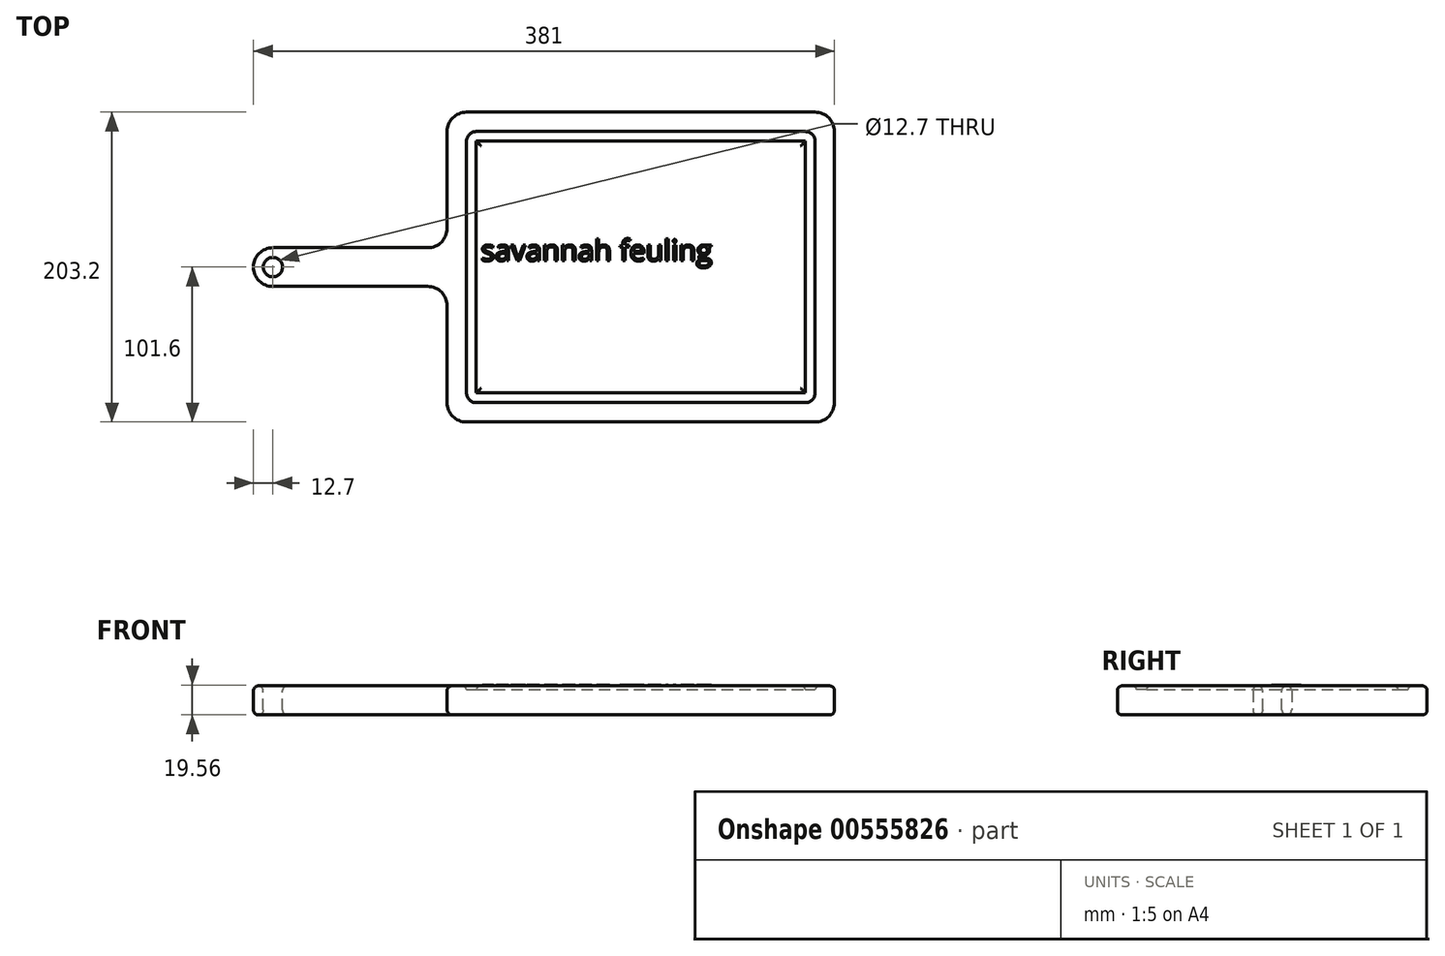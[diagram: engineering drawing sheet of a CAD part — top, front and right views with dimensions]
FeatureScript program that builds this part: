
annotation { "Feature Type Name" : "Feature", "Feature Type Description" : "" }
export const myFeature = defineFeature(function(context is Context, id is Id, definition is map)
    precondition{}
    {
        {
            var Q0;
            Q0=qCreatedBy(makeId("Top.planeOp"),FACE);
            var sketch = newSketch(context, id + "F0", { "sketchPlane" : qUnion([Q0])});
            skLineSegment(sketch, "E0.bottom", {"start": v(0, 0) * mm, "end": v(254, 0) * mm});
            skLineSegment(sketch, "E0.top", {"start": v(0, 203.2) * mm, "end": v(254, 203.2) * mm});
            skLineSegment(sketch, "E0.left", {"start": v(0, 0) * mm, "end": v(0, 203.2) * mm});
            skLineSegment(sketch, "E0.right", {"start": v(254, 0) * mm, "end": v(254, 203.2) * mm});
            skLineSegment(sketch, "E1.bottom", {"start": v(0, 114.3) * mm, "end": v(-127, 114.3) * mm});
            skLineSegment(sketch, "E1.top", {"start": v(0, 88.9) * mm, "end": v(-127, 88.9) * mm});
            skLineSegment(sketch, "E1.left", {"start": v(0, 114.3) * mm, "end": v(0, 88.9) * mm});
            skLineSegment(sketch, "E1.right", {"start": v(-127, 114.3) * mm, "end": v(-127, 88.9) * mm});
            skSolve(sketch);
        }
        {
            var Q0;
            {var subQ3=sQuery(id+"F0.wireOp",EDGE,"E0.bottom");Q0=makeQuery(id+"F0.imprint","IMPRINT",FACE,{"disambiguationData":[TD([[makeQuery(id+"F0.imprint","IMPRINT",EDGE,{"derivedFrom":subQ3}),1.0]])]});}
            var Q1;
            Q1=makeQuery(id+"F0.imprint","IMPRINT",FACE,{"disambiguationData":[TD([[makeQuery(id+"F0.imprint","IMPRINT",EDGE,{"derivedFrom":sQuery(id+"F0.wireOp",EDGE,"E1.bottom")}),1.0]])]});
            extrude(context, id + "F1", {"entities" : qUnion([Q0, Q1]), "depth" : 19.05 * mm, "offsetDistance" : 25.4 * mm});
        }
        {
            var Q0;
            Q0=makeQuery(id+"F1.opExtrude","CAP_FACE",FACE,{"disambiguationData":[OSD([sQuery(id+"F0.wireOp",EDGE,"E0.bottom"),sQuery(id+"F0.wireOp",EDGE,"E0.top"),sQuery(id+"F0.wireOp",EDGE,"E0.left"),sQuery(id+"F0.wireOp",EDGE,"E0.right"),sQuery(id+"F0.wireOp",EDGE,"E1.bottom"),sQuery(id+"F0.wireOp",EDGE,"E1.top"),sQuery(id+"F0.wireOp",EDGE,"E1.right")])],"isStart":false});
            var sketch = newSketch(context, id + "F2", { "sketchPlane" : qUnion([Q0])});
            skCircle(sketch, "E2", {"center": v(-114.3, 101.6) * mm, "radius": 6.35 * mm});
            skSolve(sketch);
        }
        {
            var Q0;
            Q0 = qSketchRegion(id + "F2", true);
            extrude(context, id + "F3", {"entities" : qUnion([Q0]), "operationType" : NewBodyOperationType.REMOVE, "oppositeDirection" : true, "depth" : 25.4 * mm, "offsetDistance" : 25.4 * mm});
        }
        {
            var Q0;
            Q0=makeQuery(id+"F1.opExtrude","CAP_FACE",FACE,{"disambiguationData":[OSD([sQuery(id+"F0.wireOp",EDGE,"E0.bottom"),sQuery(id+"F0.wireOp",EDGE,"E0.top"),sQuery(id+"F0.wireOp",EDGE,"E0.left"),sQuery(id+"F0.wireOp",EDGE,"E0.right"),sQuery(id+"F0.wireOp",EDGE,"E1.bottom"),sQuery(id+"F0.wireOp",EDGE,"E1.top"),sQuery(id+"F0.wireOp",EDGE,"E1.right")])],"isStart":false});
            var sketch = newSketch(context, id + "F4", { "sketchPlane" : qUnion([Q0])});
            skLineSegment(sketch, "E3.0", {"start": v(12.7, 12.7) * mm, "end": v(12.7, 88.9) * mm});
            skLineSegment(sketch, "E3.1", {"start": v(12.7, 114.3) * mm, "end": v(12.7, 190.5) * mm});
            skLineSegment(sketch, "E3.2", {"start": v(12.7, 190.5) * mm, "end": v(241.3, 190.5) * mm});
            skLineSegment(sketch, "E3.3", {"start": v(241.3, 12.7) * mm, "end": v(241.3, 190.5) * mm});
            skLineSegment(sketch, "E3.4", {"start": v(12.7, 12.7) * mm, "end": v(241.3, 12.7) * mm});
            skLineSegment(sketch, "E4", {"start": v(12.7, 114.3) * mm, "end": v(12.7, 88.9) * mm});
            skLineSegment(sketch, "E5.0", {"start": v(19.05, 114.3) * mm, "end": v(19.05, 184.15) * mm});
            skLineSegment(sketch, "E5.1", {"start": v(234.95, 19.05) * mm, "end": v(234.95, 184.15) * mm});
            skLineSegment(sketch, "E5.2", {"start": v(19.05, 19.05) * mm, "end": v(234.95, 19.05) * mm});
            skLineSegment(sketch, "E5.3", {"start": v(19.05, 184.15) * mm, "end": v(234.95, 184.15) * mm});
            skLineSegment(sketch, "E5.4", {"start": v(19.05, 19.05) * mm, "end": v(19.05, 88.9) * mm});
            skLineSegment(sketch, "E5.5", {"start": v(19.05, 114.3) * mm, "end": v(19.05, 88.9) * mm});
            skSolve(sketch);
        }
        {
            var Q0;
            Q0=makeQuery(id+"F4.imprint","IMPRINT",FACE,{"disambiguationData":[TD([[makeQuery(id+"F4.imprint","IMPRINT",EDGE,{"derivedFrom":sQuery(id+"F4.wireOp",EDGE,"E3.0")}),-1.0]])]});
            extrude(context, id + "F5", {"entities" : qUnion([Q0]), "operationType" : NewBodyOperationType.REMOVE, "oppositeDirection" : true, "depth" : 2.54 * mm, "offsetDistance" : 25.4 * mm});
        }
        {
            var Q0;
            Q0=makeQuery(id+"F5.boolean.opBoolean","COPY",EDGE,{"derivedFrom":makeQuery(id+"F5.opExtrude","SWEPT_EDGE",EDGE,{"disambiguationData":[OSD([sQuery(id+"F4.wireOp",EDGE,"E3.1"),sQuery(id+"F4.wireOp",EDGE,"E3.2")])]})});
            var Q1;
            Q1=makeQuery(id+"F5.boolean.opBoolean","COPY",EDGE,{"derivedFrom":makeQuery(id+"F5.opExtrude","SWEPT_EDGE",EDGE,{"disambiguationData":[OSD([sQuery(id+"F4.wireOp",EDGE,"E3.2"),sQuery(id+"F4.wireOp",EDGE,"E3.3")])]})});
            var Q2;
            Q2=makeQuery(id+"F5.boolean.opBoolean","COPY",EDGE,{"derivedFrom":makeQuery(id+"F5.opExtrude","SWEPT_EDGE",EDGE,{"disambiguationData":[OSD([sQuery(id+"F4.wireOp",EDGE,"E3.3"),sQuery(id+"F4.wireOp",EDGE,"E3.4")])]})});
            var Q3;
            Q3=makeQuery(id+"F5.boolean.opBoolean","COPY",EDGE,{"derivedFrom":makeQuery(id+"F5.opExtrude","SWEPT_EDGE",EDGE,{"disambiguationData":[OSD([sQuery(id+"F4.wireOp",EDGE,"E3.0"),sQuery(id+"F4.wireOp",EDGE,"E3.4")])]})});
            fillet(context, id + "F6", {"entities" : qUnion([Q0, Q1, Q2, Q3]), "radius" : 6.35 * mm, "tangentPropagation" : true, "allowEdgeOverflow" : false});
        }
        {
            var Q0;
            Q0=makeQuery(id+"F1.opExtrude","SWEPT_EDGE",EDGE,{"disambiguationData":[OSD([sQuery(id+"F0.wireOp",EDGE,"E0.bottom"),sQuery(id+"F0.wireOp",EDGE,"E0.left")])]});
            var Q1;
            Q1=makeQuery(id+"F1.opExtrude","SWEPT_EDGE",EDGE,{"disambiguationData":[OSD([sQuery(id+"F0.wireOp",EDGE,"E0.bottom"),sQuery(id+"F0.wireOp",EDGE,"E0.right")])]});
            var Q2;
            Q2=makeQuery(id+"F1.opExtrude","SWEPT_EDGE",EDGE,{"disambiguationData":[OSD([sQuery(id+"F0.wireOp",EDGE,"E0.top"),sQuery(id+"F0.wireOp",EDGE,"E0.right")])]});
            var Q3;
            Q3=makeQuery(id+"F1.opExtrude","SWEPT_EDGE",EDGE,{"disambiguationData":[OSD([sQuery(id+"F0.wireOp",EDGE,"E0.top"),sQuery(id+"F0.wireOp",EDGE,"E0.left")])]});
            var Q4;
            Q4=makeQuery(id+"F1.opExtrude","SWEPT_EDGE",EDGE,{"disambiguationData":[OSD([sQuery(id+"F0.wireOp",EDGE,"E1.bottom"),sQuery(id+"F0.wireOp",EDGE,"E1.right")])]});
            var Q5;
            Q5=makeQuery(id+"F1.opExtrude","SWEPT_EDGE",EDGE,{"disambiguationData":[OSD([sQuery(id+"F0.wireOp",EDGE,"E1.top"),sQuery(id+"F0.wireOp",EDGE,"E1.right")])]});
            var Q6;
            Q6=makeQuery(id+"F1.opExtrude","SWEPT_EDGE",EDGE,{"disambiguationData":[OSD([sQuery(id+"F0.wireOp",EDGE,"E0.left"),sQuery(id+"F0.wireOp",EDGE,"E1.top"),sQuery(id+"F0.wireOp",EDGE,"E1.left")])]});
            var Q7;
            Q7=makeQuery(id+"F1.opExtrude","SWEPT_EDGE",EDGE,{"disambiguationData":[OSD([sQuery(id+"F0.wireOp",EDGE,"E0.left"),sQuery(id+"F0.wireOp",EDGE,"E1.bottom"),sQuery(id+"F0.wireOp",EDGE,"E1.left")])]});
            fillet(context, id + "F7", {"entities" : qUnion([Q0, Q1, Q2, Q3, Q4, Q5, Q6, Q7]), "radius" : 12.7 * mm, "tangentPropagation" : true, "allowEdgeOverflow" : false});
        }
        {
            var Q0;
            Q0=makeQuery(id+"F5.boolean.opBoolean","SPLIT",FACE,{"disambiguationData":[TD([makeQuery(id+"F5.opExtrude","SWEPT_FACE",FACE,{"disambiguationData":[OSD([sQuery(id+"F4.wireOp",EDGE,"E5.1")])]})])],"derivedFrom":makeQuery(id+"F1.opExtrude","CAP_FACE",FACE,{"disambiguationData":[OSD([sQuery(id+"F0.wireOp",EDGE,"E0.bottom"),sQuery(id+"F0.wireOp",EDGE,"E0.top"),sQuery(id+"F0.wireOp",EDGE,"E0.left"),sQuery(id+"F0.wireOp",EDGE,"E0.right"),sQuery(id+"F0.wireOp",EDGE,"E1.bottom"),sQuery(id+"F0.wireOp",EDGE,"E1.top"),sQuery(id+"F0.wireOp",EDGE,"E1.right")])],"isStart":false})});
            var Q1;
            {var subQ0=sQuery(id+"F0.wireOp",EDGE,"E1.right");var subQ1=sQuery(id+"F0.wireOp",EDGE,"E1.top");var subQ2=sQuery(id+"F0.wireOp",EDGE,"E1.bottom");var subQ3=sQuery(id+"F0.wireOp",EDGE,"E0.right");var subQ4=sQuery(id+"F0.wireOp",EDGE,"E0.bottom");var subQ5=sQuery(id+"F0.wireOp",EDGE,"E0.left");var subQ6=sQuery(id+"F0.wireOp",EDGE,"E0.top");Q1=makeQuery(id+"F5.boolean.opBoolean","SPLIT",FACE,{"disambiguationData":[TD([makeQuery(id+"F1.opExtrude","SWEPT_FACE",FACE,{"disambiguationData":[OSD([subQ4])]})])],"derivedFrom":makeQuery(id+"F1.opExtrude","CAP_FACE",FACE,{"disambiguationData":[OSD([subQ4,subQ6,subQ5,subQ3,subQ2,subQ1,subQ0])],"isStart":false})});}
            var Q2;
            Q2=makeQuery(id+"F1.opExtrude","CAP_FACE",FACE,{"disambiguationData":[OSD([sQuery(id+"F0.wireOp",EDGE,"E0.bottom"),sQuery(id+"F0.wireOp",EDGE,"E0.top"),sQuery(id+"F0.wireOp",EDGE,"E0.left"),sQuery(id+"F0.wireOp",EDGE,"E0.right"),sQuery(id+"F0.wireOp",EDGE,"E1.bottom"),sQuery(id+"F0.wireOp",EDGE,"E1.top"),sQuery(id+"F0.wireOp",EDGE,"E1.right")])],"isStart":true});
            fillet(context, id + "F8", {"entities" : qUnion([Q0, Q1, Q2]), "radius" : 3.17 * mm, "tangentPropagation" : true, "allowEdgeOverflow" : false});
        }
        {
            var Q0;
            Q0=makeQuery(id+"F5.boolean.opBoolean","SPLIT",FACE,{"disambiguationData":[TD([makeQuery(id+"F5.opExtrude","SWEPT_FACE",FACE,{"disambiguationData":[OSD([sQuery(id+"F4.wireOp",EDGE,"E5.1")])]})])],"derivedFrom":makeQuery(id+"F1.opExtrude","CAP_FACE",FACE,{"disambiguationData":[OSD([sQuery(id+"F0.wireOp",EDGE,"E0.bottom"),sQuery(id+"F0.wireOp",EDGE,"E0.top"),sQuery(id+"F0.wireOp",EDGE,"E0.left"),sQuery(id+"F0.wireOp",EDGE,"E0.right"),sQuery(id+"F0.wireOp",EDGE,"E1.bottom"),sQuery(id+"F0.wireOp",EDGE,"E1.top"),sQuery(id+"F0.wireOp",EDGE,"E1.right")])],"isStart":false})});
            var sketch = newSketch(context, id + "F9", { "sketchPlane" : qUnion([Q0])});
            skText(sketch, "E6", { "text": "savannah feuling", "fontName": "OpenSans-Regular.ttf"});
            const initialGuessF9  = {"E6": [0.02216, 0.10572, 1, 0, 0.01377]};
            skSetInitialGuess(sketch, initialGuessF9);
            skSolve(sketch);
        }
        {
            var Q0;
            Q0 = qSketchRegion(id + "F9", true);
            extrude(context, id + "F10", {"entities" : qUnion([Q0]), "operationType" : NewBodyOperationType.ADD, "depth" : 0.5 * mm, "offsetDistance" : 25.4 * mm});
        }
    });
